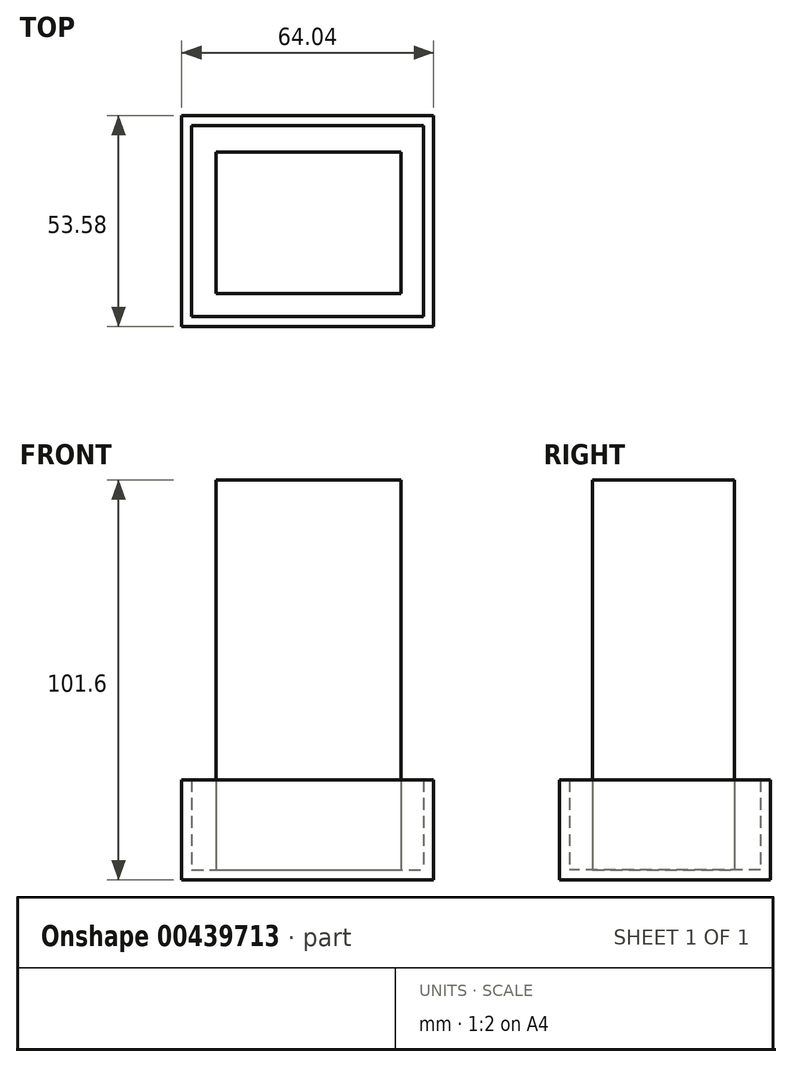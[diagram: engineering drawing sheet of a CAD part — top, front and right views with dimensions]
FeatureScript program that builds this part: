
annotation { "Feature Type Name" : "Feature", "Feature Type Description" : "" }
export const myFeature = defineFeature(function(context is Context, id is Id, definition is map)
    precondition{}
    {
        {
            var Q0;
            Q0=qCreatedBy(makeId("Top.planeOp"),FACE);
            var sketch = newSketch(context, id + "F0", { "sketchPlane" : qUnion([Q0])});
            skLineSegment(sketch, "E0.bottom", {"start": v(-17.86, 28.1) * mm, "end": v(46.18, 28.1) * mm});
            skLineSegment(sketch, "E0.top", {"start": v(-17.86, -25.48) * mm, "end": v(46.18, -25.48) * mm});
            skLineSegment(sketch, "E0.left", {"start": v(-17.86, 28.1) * mm, "end": v(-17.86, -25.48) * mm});
            skLineSegment(sketch, "E0.right", {"start": v(46.18, 28.1) * mm, "end": v(46.18, -25.48) * mm});
            skSolve(sketch);
        }
        {
            var Q0;
            Q0=makeQuery(id+"F0.imprint","IMPRINT",FACE,{"disambiguationData":[TD([[makeQuery(id+"F0.imprint","IMPRINT",EDGE,{"derivedFrom":sQuery(id+"F0.wireOp",EDGE,"E0.bottom")}),-1.0]])]});
            extrude(context, id + "F1", {"entities" : qUnion([Q0]), "depth" : 25.4 * mm});
        }
        {
            var Q0;
            Q0=makeQuery(id+"F1.opExtrude","CAP_FACE",FACE,{"disambiguationData":[OSD([sQuery(id+"F0.wireOp",EDGE,"E0.bottom"),sQuery(id+"F0.wireOp",EDGE,"E0.top"),sQuery(id+"F0.wireOp",EDGE,"E0.left"),sQuery(id+"F0.wireOp",EDGE,"E0.right")])],"isStart":false});
            shell(context, id + "F2", {"entities" : qUnion([Q0]), "thickness" : 2.54 * mm});
        }
        {
            var Q0;
            Q0=qCreatedBy(makeId("Top.planeOp"),FACE);
            var sketch = newSketch(context, id + "F3", { "sketchPlane" : qUnion([Q0])});
            skLineSegment(sketch, "E1.bottom", {"start": v(37.88, 18.88) * mm, "end": v(-9.09, 18.88) * mm});
            skLineSegment(sketch, "E1.top", {"start": v(37.88, -17.12) * mm, "end": v(-9.09, -17.12) * mm});
            skLineSegment(sketch, "E1.left", {"start": v(37.88, 18.88) * mm, "end": v(37.88, -17.12) * mm});
            skLineSegment(sketch, "E1.right", {"start": v(-9.09, 18.88) * mm, "end": v(-9.09, -17.12) * mm});
            skSolve(sketch);
        }
        {
            var Q0;
            Q0 = qSketchRegion(id + "F3", true);
            extrude(context, id + "F4", {"entities" : qUnion([Q0]), "operationType" : NewBodyOperationType.ADD, "depth" : 76.2 * mm});
        }
        {
            var Q0;
            Q0=makeQuery(id+"F4.opExtrude","CAP_FACE",FACE,{"disambiguationData":[OSD([sQuery(id+"F3.wireOp",EDGE,"E1.bottom"),sQuery(id+"F3.wireOp",EDGE,"E1.top"),sQuery(id+"F3.wireOp",EDGE,"E1.left"),sQuery(id+"F3.wireOp",EDGE,"E1.right")])],"isStart":false});
            var sketch = newSketch(context, id + "F5", { "sketchPlane" : qUnion([Q0])});
            skLineSegment(sketch, "E2.bottom", {"start": v(37.88, 18.88) * mm, "end": v(-9.09, 18.88) * mm});
            skLineSegment(sketch, "E2.top", {"start": v(37.88, -17.12) * mm, "end": v(-9.09, -17.12) * mm});
            skLineSegment(sketch, "E2.left", {"start": v(37.88, 18.88) * mm, "end": v(37.88, -17.12) * mm});
            skLineSegment(sketch, "E2.right", {"start": v(-9.09, 18.88) * mm, "end": v(-9.09, -17.12) * mm});
            skSolve(sketch);
        }
        {
            var Q0;
            Q0 = qSketchRegion(id + "F5", true);
            extrude(context, id + "F6", {"entities" : qUnion([Q0]), "operationType" : NewBodyOperationType.ADD, "depth" : 25.4 * mm});
        }
    });
